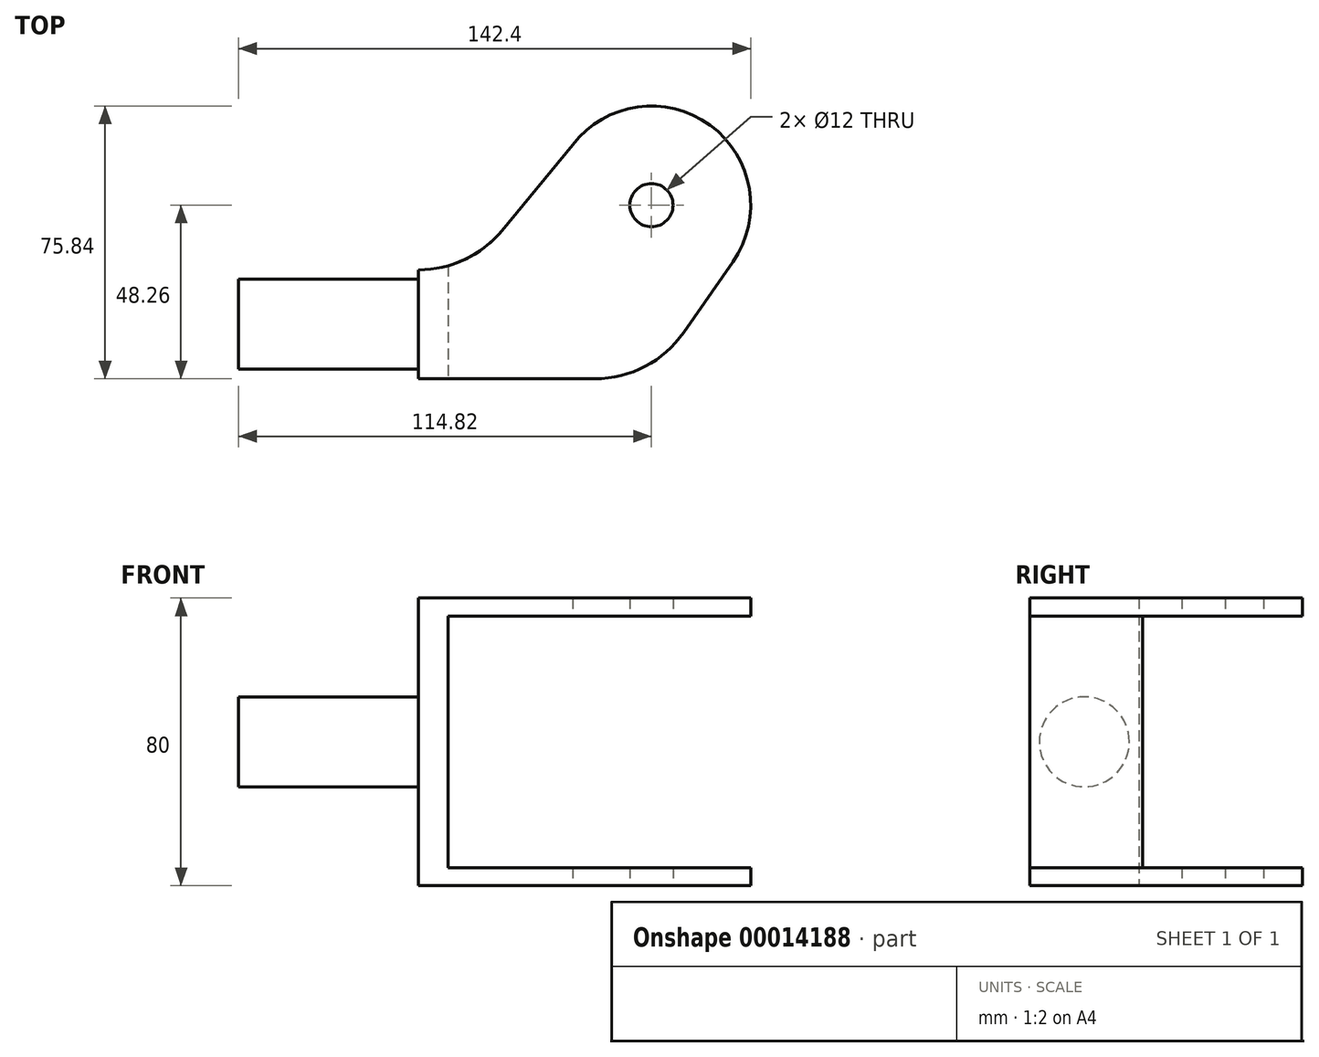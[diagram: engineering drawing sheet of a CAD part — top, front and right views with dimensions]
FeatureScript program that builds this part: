
annotation { "Feature Type Name" : "Feature", "Feature Type Description" : "" }
export const myFeature = defineFeature(function(context is Context, id is Id, definition is map)
    precondition{}
    {
        {
            var Q0;
            Q0=qCreatedBy(makeId("Top.planeOp"),FACE);
            var sketch = newSketch(context, id + "F0", { "sketchPlane" : qUnion([Q0])});
            skCircle(sketch, "E0", {"center": v(0, 0) * mm, "radius": 6 * mm});
            skLineSegment(sketch, "E1.top", {"start": v(-15.67, -48.26) * mm, "end": v(-64.82, -48.26) * mm});
            skLineSegment(sketch, "E1.right", {"start": v(-64.82, -18) * mm, "end": v(-64.82, -48.26) * mm});
            skArc(sketch, "E2", {"start": v(22.63, -15.76) * mm, "mid": v(16.28, 22.26) * mm, "end": v(-21.88, 16.79) * mm});
            skLineSegment(sketch, "E3", {"start": v(-21.88, 16.79) * mm, "end": v(-41.62, -7.1) * mm});
            skLineSegment(sketch, "E4", {"start": v(8.95, -35.4) * mm, "end": v(22.63, -15.76) * mm});
            skLineSegment(sketch, "E5.trimOffspring", {"start": v(-64.75, -18) * mm, "end": v(-64.82, -18) * mm});
            skPoint(sketch, "E6.visualSharp", {"position": v(-50.62, -18) * mm});
            skArc(sketch, "E6.filletArc", {"start": v(-64.75, -18) * mm, "mid": v(-51.96, -15.14) * mm, "end": v(-41.62, -7.1) * mm});
            skPoint(sketch, "E7.visualSharp", {"position": v(0, -48.26) * mm});
            skArc(sketch, "E7.filletArc", {"start": v(-15.67, -48.26) * mm, "mid": v(-1.78, -44.85) * mm, "end": v(8.95, -35.4) * mm});
            skSolve(sketch);
        }
        {
            var Q0;
            Q0=qSketchRegion(id+"F0",true);
            extrude(context, id + "F1", {"entities" : qUnion([Q0]), "depth" : 80 * mm});
        }
        {
            var Q0;
            Q0=makeQuery(id+"F1.opExtrude","SWEPT_FACE",FACE,{"disambiguationData":[OSD([sQuery(id+"F0.wireOp",EDGE,"E1.right")])]});
            var sketch = newSketch(context, id + "F2", { "sketchPlane" : qUnion([Q0])});
            skCircle(sketch, "E8", {"center": v(33.13, 40) * mm, "radius": 12.5 * mm});
            skSolve(sketch);
        }
        {
            var Q0;
            Q0 = qSketchRegion(id + "F2", true);
            extrude(context, id + "F3", {"entities" : qUnion([Q0]), "operationType" : NewBodyOperationType.ADD, "depth" : 50 * mm});
        }
        {
            var Q0;
            Q0=makeQuery(id+"F1.opExtrude","SWEPT_FACE",FACE,{"disambiguationData":[OSD([sQuery(id+"F0.wireOp",EDGE,"E1.top")])]});
            var sketch = newSketch(context, id + "F4", { "sketchPlane" : qUnion([Q0])});
            skLineSegment(sketch, "E9.bottom", {"start": v(47.87, 75) * mm, "end": v(-56.57, 75) * mm});
            skLineSegment(sketch, "E9.top", {"start": v(47.87, 5) * mm, "end": v(-56.57, 5) * mm});
            skLineSegment(sketch, "E9.left", {"start": v(47.87, 75) * mm, "end": v(47.87, 5) * mm});
            skLineSegment(sketch, "E9.right", {"start": v(-56.57, 75) * mm, "end": v(-56.57, 5) * mm});
            skSolve(sketch);
        }
        {
            var Q0;
            Q0 = qSketchRegion(id + "F4", true);
            extrude(context, id + "F5", {"entities" : qUnion([Q0]), "operationType" : NewBodyOperationType.REMOVE, "endBound" : BoundingType.THROUGH_ALL, "oppositeDirection" : true, "depth" : 25 * mm});
        }
    });
